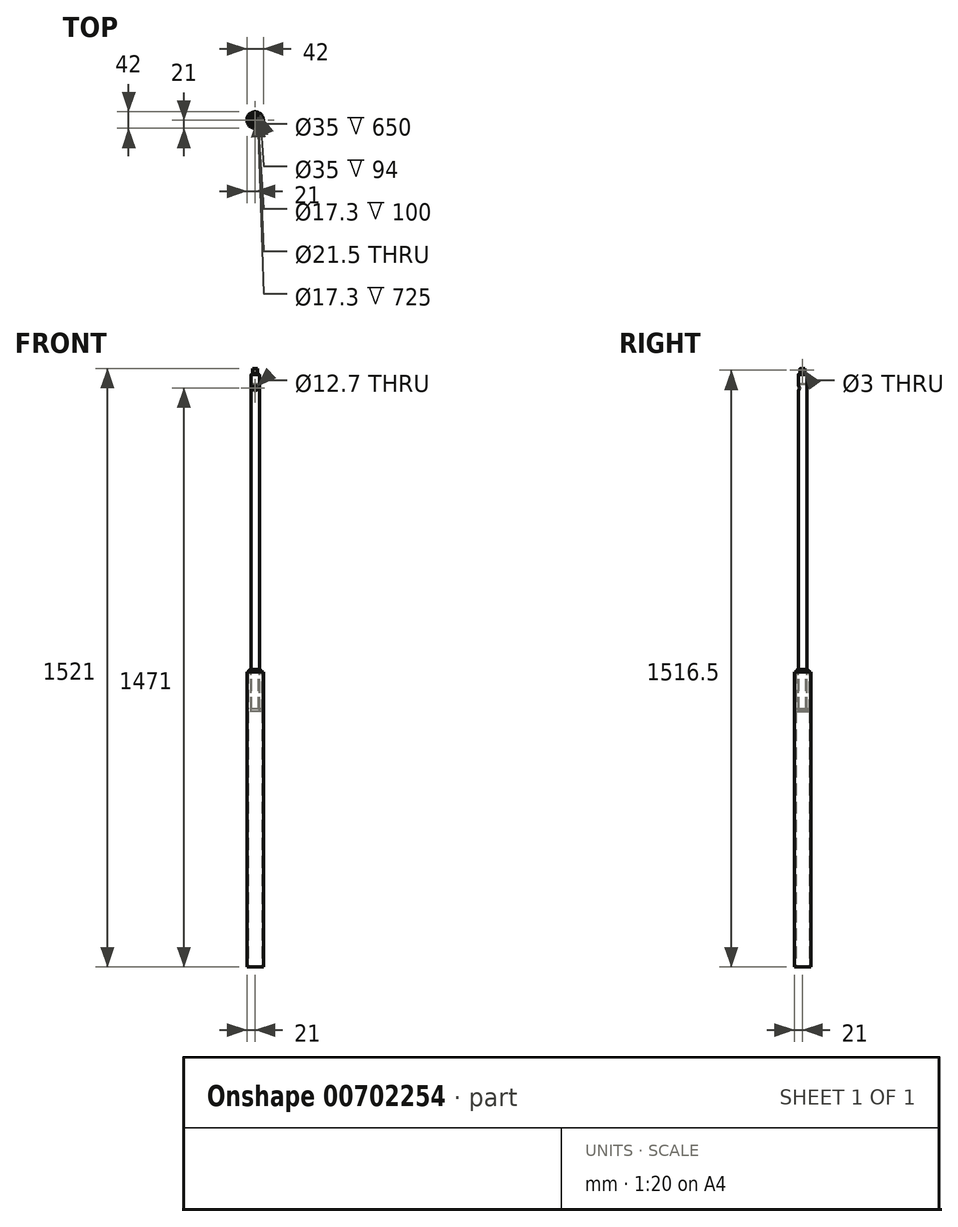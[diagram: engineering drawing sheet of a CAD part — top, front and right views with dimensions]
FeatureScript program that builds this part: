
annotation { "Feature Type Name" : "Feature", "Feature Type Description" : "" }
export const myFeature = defineFeature(function(context is Context, id is Id, definition is map)
    precondition{}
    {
        {
            var Q0;
            Q0=qCreatedBy(makeId("Top.planeOp"),FACE);
            var sketch = newSketch(context, id + "F0", { "sketchPlane" : qUnion([Q0])});
            skCircle(sketch, "E0", {"center": v(0, 0) * mm, "radius": 21 * mm});
            skCircle(sketch, "E1", {"center": v(0, 0) * mm, "radius": 17.5 * mm});
            skSolve(sketch);
        }
        {
            var Q0;
            Q0 = qSketchRegion(id + "F0", true);
            extrude(context, id + "F1", {"entities" : qUnion([Q0]), "depth" : 750 * mm, "offsetDistance" : 25 * mm});
        }
        {
            var Q0;
            Q0=makeQuery(id+"F1.opExtrude","CAP_FACE",FACE,{"disambiguationData":[OSD([sQuery(id+"F0.wireOp",EDGE,"E0"),sQuery(id+"F0.wireOp",EDGE,"E1")])],"isStart":false});
            var sketch = newSketch(context, id + "F2", { "sketchPlane" : qUnion([Q0])});
            skCircle(sketch, "E2.0", {"center": v(0, 0) * mm, "radius": 17.5 * mm});
            skSolve(sketch);
        }
        {
            var Q0;
            Q0 = qSketchRegion(id + "F2", true);
            extrude(context, id + "F3", {"entities" : qUnion([Q0]), "operationType" : NewBodyOperationType.ADD, "depth" : 6 * mm, "offsetDistance" : 25 * mm});
        }
        {
            var Q0;
            Q0=makeQuery(id+"F3.opExtrude","CAP_FACE",FACE,{"disambiguationData":[OSD([sQuery(id+"F2.wireOp",EDGE,"E2.0")])],"isStart":false});
            var sketch = newSketch(context, id + "F4", { "sketchPlane" : qUnion([Q0])});
            skCircle(sketch, "E3", {"center": v(0, 0) * mm, "radius": 10.65 * mm});
            skCircle(sketch, "E4", {"center": v(0, 0) * mm, "radius": 8.65 * mm});
            skSolve(sketch);
        }
        {
            var Q0;
            Q0=makeQuery(id+"F4.imprint","IMPRINT",FACE,{"disambiguationData":[TD([[makeQuery(id+"F4.imprint","IMPRINT",EDGE,{"derivedFrom":sQuery(id+"F4.wireOp",EDGE,"E3")}),1.0]])]});
            extrude(context, id + "F5", {"entities" : qUnion([Q0]), "depth" : 750 * mm, "offsetDistance" : 25 * mm});
        }
        {
            var Q0;
            Q0=makeQuery(id+"F3.opExtrude","CAP_FACE",FACE,{"disambiguationData":[OSD([sQuery(id+"F2.wireOp",EDGE,"E2.0")])],"isStart":false});
            var sketch = newSketch(context, id + "F6", { "sketchPlane" : qUnion([Q0])});
            skCircle(sketch, "E5.0", {"center": v(0, 0) * mm, "radius": 10.65 * mm});
            skCircle(sketch, "E6.0", {"center": v(0, 0) * mm, "radius": 8.65 * mm});
            skSolve(sketch);
        }
        {
            var Q0;
            Q0 = qSketchRegion(id + "F6", true);
            extrude(context, id + "F7", {"entities" : qUnion([Q0]), "oppositeDirection" : true, "depth" : 100 * mm, "offsetDistance" : 25 * mm});
        }
        {
            var Q0;
            Q0=qCreatedBy(makeId("Top.planeOp"),FACE);
            cPlane(context, id + "F8", {"entities" : qUnion([Q0]), "cplaneType" : CPlaneType.OFFSET, "offset" : 650 * mm, "width" : 150 * mm, "height" : 150 * mm});
        }
        {
            var Q0;
            Q0=qCreatedBy(id+"F8.planeOp",FACE);
            var sketch = newSketch(context, id + "F9", { "sketchPlane" : qUnion([Q0])});
            skCircle(sketch, "E7.0", {"center": v(0, 0) * mm, "radius": 17.5 * mm});
            skSolve(sketch);
        }
        {
            var Q0;
            Q0 = qSketchRegion(id + "F9", true);
            extrude(context, id + "F10", {"entities" : qUnion([Q0]), "operationType" : NewBodyOperationType.ADD, "depth" : 6 * mm, "offsetDistance" : 25 * mm});
        }
        {
            var Q0;
            Q0=makeQuery(id+"F5.opExtrude","CAP_FACE",FACE,{"disambiguationData":[OSD([sQuery(id+"F4.wireOp",EDGE,"E3"),sQuery(id+"F4.wireOp",EDGE,"E4")])],"isStart":false});
            var sketch = newSketch(context, id + "F11", { "sketchPlane" : qUnion([Q0])});
            skCircle(sketch, "E8.0", {"center": v(0, 0) * mm, "radius": 8.65 * mm});
            skSolve(sketch);
        }
        {
            var Q0;
            Q0 = qSketchRegion(id + "F11", true);
            extrude(context, id + "F12", {"entities" : qUnion([Q0]), "oppositeDirection" : true, "depth" : 25 * mm, "offsetDistance" : 25 * mm});
        }
        {
            var Q0;
            Q0=makeQuery(id+"F12.opExtrude","CAP_FACE",FACE,{"disambiguationData":[OSD([sQuery(id+"F11.wireOp",EDGE,"E8.0")])],"isStart":true});
            var sketch = newSketch(context, id + "F13", { "sketchPlane" : qUnion([Q0])});
            skCircle(sketch, "E9", {"center": v(0, 0) * mm, "radius": 6.35 * mm});
            skSolve(sketch);
        }
        {
            var Q0;
            Q0 = qSketchRegion(id + "F13", true);
            extrude(context, id + "F14", {"entities" : qUnion([Q0]), "operationType" : NewBodyOperationType.ADD, "depth" : 15 * mm, "offsetDistance" : 25 * mm});
        }
        {
            var Q0;
            Q0 = qSketchRegion(id + "F13", true);
            extrude(context, id + "F15", {"entities" : qUnion([Q0]), "operationType" : NewBodyOperationType.ADD, "depth" : 15 * mm, "offsetDistance" : 25 * mm});
        }
        {
            var Q0;
            Q0=qCreatedBy(makeId("Right.planeOp"),FACE);
            var sketch = newSketch(context, id + "F16", { "sketchPlane" : qUnion([Q0])});
            skCircle(sketch, "E10", {"center": v(0, 1516.5) * mm, "radius": 1.5 * mm});
            skSolve(sketch);
        }
        {
            var Q0;
            Q0 = qSketchRegion(id + "F16", true);
            extrude(context, id + "F17", {"entities" : qUnion([Q0]), "operationType" : NewBodyOperationType.REMOVE, "endBound" : BoundingType.SYMMETRIC, "oppositeDirection" : true, "depth" : 20 * mm, "offsetDistance" : 25 * mm});
        }
        {
            var Q0;
            Q0=makeQuery(id+"F12.opExtrude","CAP_FACE",FACE,{"disambiguationData":[OSD([sQuery(id+"F11.wireOp",EDGE,"E8.0")])],"isStart":true});
            var sketch = newSketch(context, id + "F18", { "sketchPlane" : qUnion([Q0])});
            skCircle(sketch, "E11.0", {"center": v(0, 0) * mm, "radius": 8.65 * mm});
            skCircle(sketch, "E12.0", {"center": v(0, 0) * mm, "radius": 6.35 * mm});
            skSolve(sketch);
        }
        {
            var Q0;
            Q0 = qSketchRegion(id + "F18", true);
            extrude(context, id + "F19", {"entities" : qUnion([Q0]), "operationType" : NewBodyOperationType.ADD, "depth" : 2 * mm, "offsetDistance" : 25 * mm});
        }
        {
            var Q0;
            Q0=qCreatedBy(makeId("Front.planeOp"),FACE);
            var sketch = newSketch(context, id + "F20", { "sketchPlane" : qUnion([Q0])});
            skLineSegment(sketch, "E13", {"start": v(0, 1653.23) * mm, "end": v(0, 1514.52) * mm, "construction": true});
            skCircle(sketch, "E14", {"center": v(0, 1471) * mm, "radius": 6.35 * mm});
            skSolve(sketch);
        }
        {
            var Q0;
            Q0 = qSketchRegion(id + "F20", true);
            extrude(context, id + "F21", {"entities" : qUnion([Q0]), "operationType" : NewBodyOperationType.REMOVE, "endBound" : BoundingType.THROUGH_ALL, "depth" : 25 * mm, "offsetDistance" : 25 * mm});
        }
        {
            var Q0;
            Q0=makeQuery(id+"F1.opExtrude","CAP_FACE",FACE,{"disambiguationData":[OSD([sQuery(id+"F0.wireOp",EDGE,"E0"),sQuery(id+"F0.wireOp",EDGE,"E1")])],"isStart":false});
            var sketch = newSketch(context, id + "F22", { "sketchPlane" : qUnion([Q0])});
            skCircle(sketch, "E15", {"center": v(0, 0) * mm, "radius": 17.4 * mm});
            skCircle(sketch, "E16", {"center": v(0, 0) * mm, "radius": 10.75 * mm});
            skSolve(sketch);
        }
        {
            var Q0;
            Q0 = qSketchRegion(id + "F22", true);
            extrude(context, id + "F23", {"entities" : qUnion([Q0]), "oppositeDirection" : true, "depth" : 100 * mm, "offsetDistance" : 25 * mm});
        }
        {
            var Q0;
            Q0=makeQuery(id+"F3.opExtrude","CAP_EDGE",EDGE,{"disambiguationData":[OSD([sQuery(id+"F2.wireOp",EDGE,"E2.0")])],"isStart":false});
            chamfer(context, id + "F24", {"entities" : qUnion([Q0]), "width" : 5 * mm, "tangentPropagation" : true});
        }
    });
